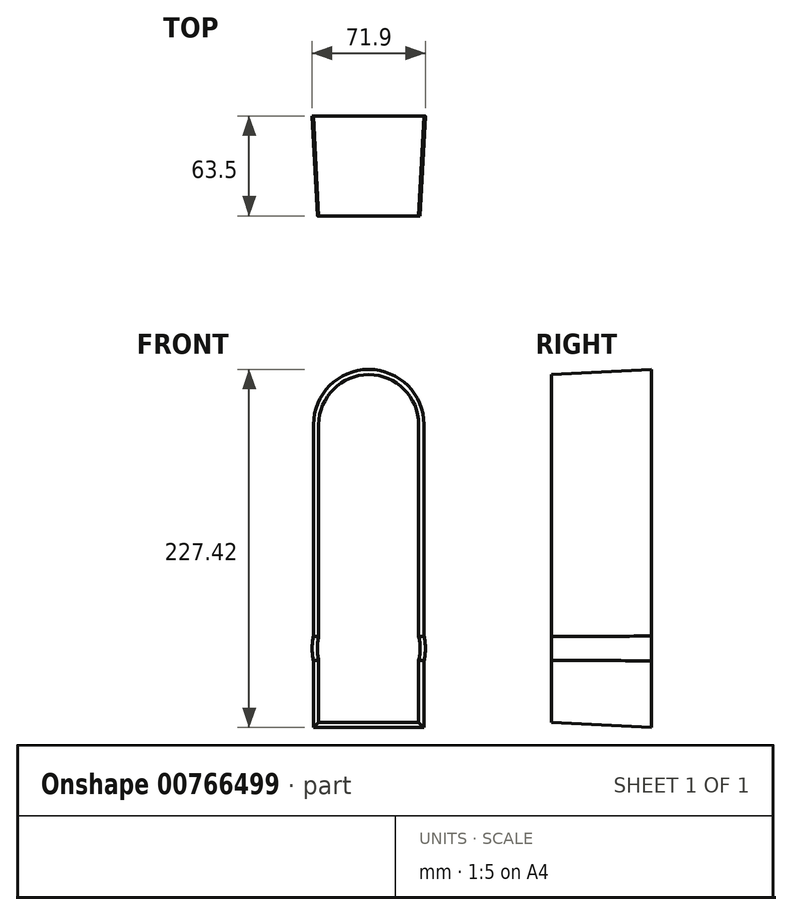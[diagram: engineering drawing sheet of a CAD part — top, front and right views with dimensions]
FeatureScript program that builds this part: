
annotation { "Feature Type Name" : "Feature", "Feature Type Description" : "" }
export const myFeature = defineFeature(function(context is Context, id is Id, definition is map)
    precondition{}
    {
        {
            var Q0;
            Q0=qCreatedBy(makeId("Front.planeOp"),FACE);
            var sketch = newSketch(context, id + "F0", { "sketchPlane" : qUnion([Q0])});
            skLineSegment(sketch, "E0.bottom", {"start": v(-43.62, 134.63) * mm, "end": v(19.88, 134.63) * mm});
            skLineSegment(sketch, "E0.top", {"start": v(-43.62, -54.38) * mm, "end": v(19.88, -54.38) * mm});
            skLineSegment(sketch, "E0.left", {"start": v(-43.62, 134.63) * mm, "end": v(-43.62, -54.38) * mm});
            skLineSegment(sketch, "E0.right", {"start": v(19.88, 134.63) * mm, "end": v(19.88, -54.38) * mm});
            skLineSegment(sketch, "E1", {"start": v(-11.87, 134.63) * mm, "end": v(-11.87, -54.38) * mm});
            skLineSegment(sketch, "E2", {"start": v(-43.62, 0) * mm, "end": v(19.88, 0) * mm, "construction": true});
            skLineSegment(sketch, "E3", {"start": v(19.88, 0) * mm, "end": v(-11.87, 134.63) * mm, "construction": true});
            skLineSegment(sketch, "E4", {"start": v(-43.62, 0) * mm, "end": v(-11.87, 134.63) * mm, "construction": true});
            skLineSegment(sketch, "E5", {"start": v(-43.62, 0) * mm, "end": v(-11.87, -7.49) * mm, "construction": true});
            skArc(sketch, "E6", {"start": v(-43.62, 134.63) * mm, "mid": v(-11.87, 166.38) * mm, "end": v(19.88, 134.63) * mm});
            skArc(sketch, "E7", {"start": v(-43.62, 0) * mm, "mid": v(-37.45, -27.73) * mm, "end": v(-11.87, -40.1) * mm});
            skLineSegment(sketch, "E8.MirrorCS", {"start": v(19.88, 0) * mm, "end": v(-11.87, -7.49) * mm, "construction": true});
            skArc(sketch, "E9.MirrorCS", {"start": v(19.88, 0) * mm, "mid": v(13.7, -27.73) * mm, "end": v(-11.87, -40.1) * mm});
            skSolve(sketch);
        }
        {
            var Q0;
            Q0 = qSketchRegion(id + "F0", true);
            extrude(context, id + "F1", {"entities" : qUnion([Q0]), "oppositeDirection" : true, "depth" : 63.5 * mm, "offsetDistance" : 25.4 * mm, "hasDraft" : true, "draftAngle" : 3 * degree});
        }
    });
